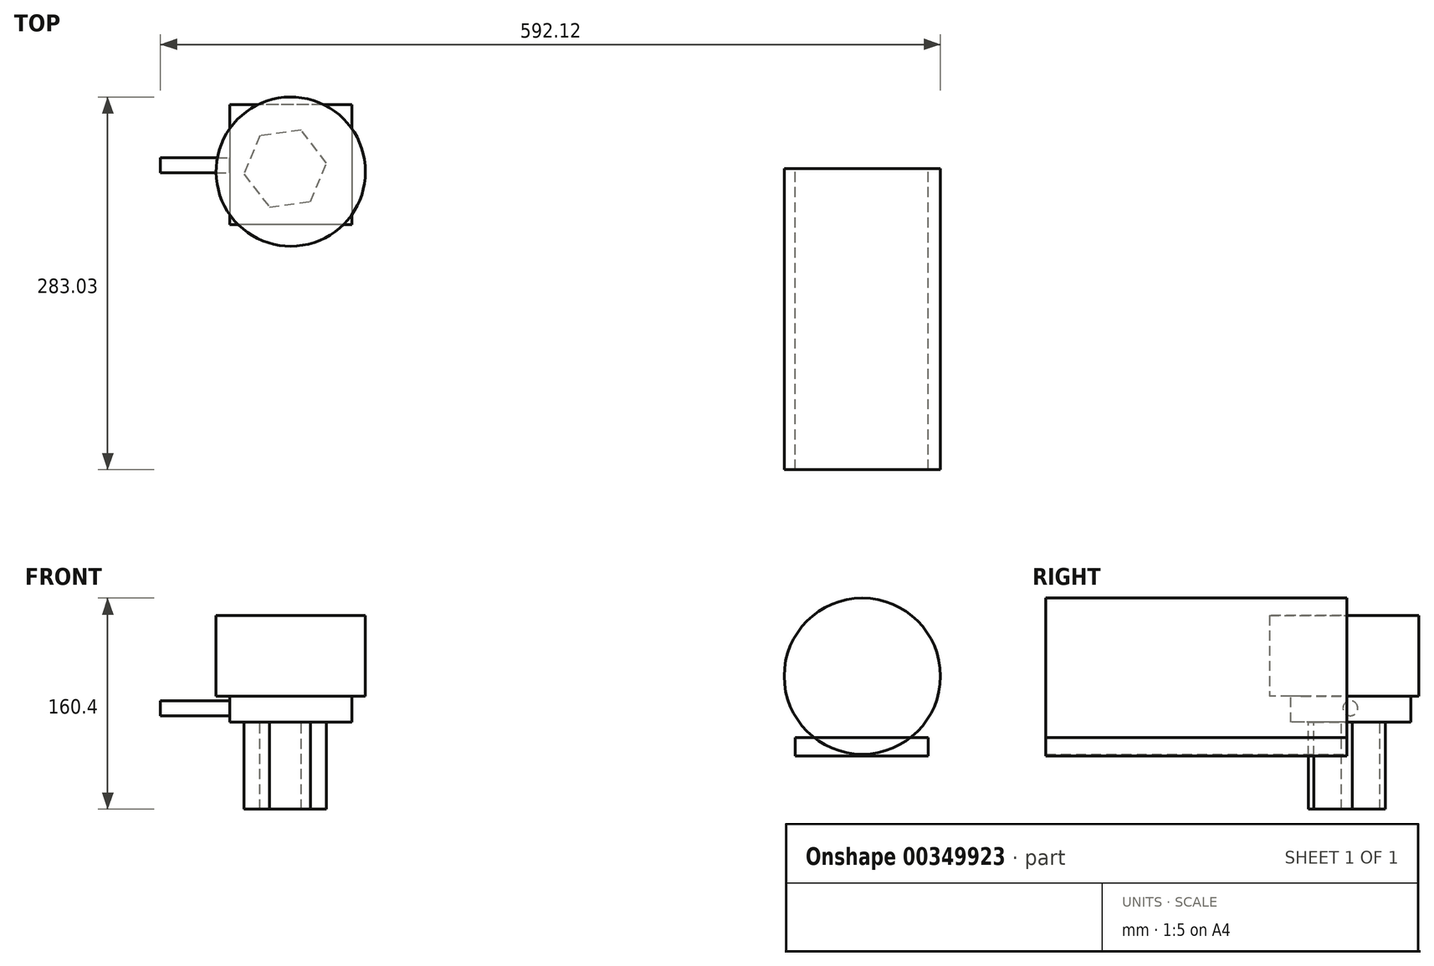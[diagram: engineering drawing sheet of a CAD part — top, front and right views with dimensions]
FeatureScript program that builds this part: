
annotation { "Feature Type Name" : "Feature", "Feature Type Description" : "" }
export const myFeature = defineFeature(function(context is Context, id is Id, definition is map)
    precondition{}
    {
        {
            var Q0;
            Q0=qCreatedBy(makeId("Top.planeOp"),FACE);
            var sketch = newSketch(context, id + "F0", { "sketchPlane" : qUnion([Q0])});
            skCircle(sketch, "E0", {"center": v(0, -2.26) * mm, "radius": 56.68 * mm});
            skSolve(sketch);
        }
        {
            var Q0;
            Q0 = qSketchRegion(id + "F0", true);
            extrude(context, id + "F1", {"entities" : qUnion([Q0]), "depth" : 61.2 * mm, "offsetDistance" : 25.4 * mm});
        }
        {
            var Q0;
            Q0=makeQuery(id+"F1.opExtrude","CAP_FACE",FACE,{"disambiguationData":[OSD([sQuery(id+"F0.wireOp",EDGE,"E0")])],"isStart":true});
            var sketch = newSketch(context, id + "F2", { "sketchPlane" : qUnion([Q0])});
            skLineSegment(sketch, "E1.bottom", {"start": v(46.36, -48.45) * mm, "end": v(-46.36, -48.45) * mm});
            skLineSegment(sketch, "E1.top", {"start": v(46.36, 42.65) * mm, "end": v(-46.36, 42.65) * mm});
            skLineSegment(sketch, "E1.left", {"start": v(46.36, -48.45) * mm, "end": v(46.36, 42.65) * mm});
            skLineSegment(sketch, "E1.right", {"start": v(-46.36, -48.45) * mm, "end": v(-46.36, 42.65) * mm});
            skPoint(sketch, "E1.middle", {"position": v(0, -2.9) * mm});
            skSolve(sketch);
        }
        {
            var Q0;
            Q0 = qSketchRegion(id + "F2", true);
            extrude(context, id + "F3", {"entities" : qUnion([Q0]), "operationType" : NewBodyOperationType.ADD, "depth" : 19.8 * mm, "offsetDistance" : 25.4 * mm});
        }
        {
            var Q0;
            Q0=makeQuery(id+"F3.opExtrude","SWEPT_FACE",FACE,{"disambiguationData":[OSD([sQuery(id+"F2.wireOp",EDGE,"E1.right")])]});
            var sketch = newSketch(context, id + "F4", { "sketchPlane" : qUnion([Q0])});
            skCircle(sketch, "E2", {"center": v(-2.6, -9.2) * mm, "radius": 5.68 * mm});
            skSolve(sketch);
        }
        {
            var Q0;
            Q0 = qSketchRegion(id + "F4", true);
            extrude(context, id + "F5", {"entities" : qUnion([Q0]), "operationType" : NewBodyOperationType.ADD, "depth" : 52.58 * mm, "offsetDistance" : 25.4 * mm});
        }
        {
            var Q0;
            Q0=makeQuery(id+"F3.opExtrude","CAP_FACE",FACE,{"disambiguationData":[OSD([sQuery(id+"F2.wireOp",EDGE,"E1.bottom"),sQuery(id+"F2.wireOp",EDGE,"E1.top"),sQuery(id+"F2.wireOp",EDGE,"E1.left"),sQuery(id+"F2.wireOp",EDGE,"E1.right")])],"isStart":false});
            var sketch = newSketch(context, id + "F6", { "sketchPlane" : qUnion([Q0])});
            skCircle(sketch, "E3.cCircle", {"center": v(-4.2, 0) * mm, "radius": 27.37 * mm, "construction": true});
            skLineSegment(sketch, "E3.0", {"start": v(27.13, -4.2) * mm, "end": v(7.83, -29.23) * mm});
            skLineSegment(sketch, "E3.1", {"start": v(7.83, -29.23) * mm, "end": v(-23.5, -25.02) * mm});
            skLineSegment(sketch, "E3.2", {"start": v(-23.5, -25.02) * mm, "end": v(-35.51, 4.2) * mm});
            skLineSegment(sketch, "E3.3", {"start": v(-35.51, 4.2) * mm, "end": v(-16.21, 29.23) * mm});
            skLineSegment(sketch, "E3.4", {"start": v(-16.21, 29.23) * mm, "end": v(15.11, 25.02) * mm});
            skLineSegment(sketch, "E3.5", {"start": v(15.11, 25.02) * mm, "end": v(27.13, -4.2) * mm});
            skPoint(sketch, "E3.0.midPoint", {"position": v(17.48, -16.72) * mm});
            skSolve(sketch);
        }
        {
            var Q0;
            Q0 = qSketchRegion(id + "F6", true);
            extrude(context, id + "F7", {"entities" : qUnion([Q0]), "operationType" : NewBodyOperationType.ADD, "depth" : 66.04 * mm, "offsetDistance" : 25.4 * mm});
        }
        {
            var Q0;
            Q0=qCreatedBy(makeId("Front.planeOp"),FACE);
            var sketch = newSketch(context, id + "F8", { "sketchPlane" : qUnion([Q0])});
            skCircle(sketch, "E4", {"center": v(258.37, 0) * mm, "radius": 59.3 * mm});
            skLineSegment(sketch, "E5.bottom", {"start": v(382.95, -31.55) * mm, "end": v(484, -31.55) * mm});
            skLineSegment(sketch, "E5.top", {"start": v(382.95, -45.28) * mm, "end": v(484, -45.28) * mm});
            skLineSegment(sketch, "E5.left", {"start": v(382.95, -31.55) * mm, "end": v(382.95, -45.28) * mm});
            skLineSegment(sketch, "E5.right", {"start": v(484, -31.55) * mm, "end": v(484, -45.28) * mm});
            skSolve(sketch);
        }
        {
            var Q0;
            Q0 = qSketchRegion(id + "F8", true);
            extrude(context, id + "F9", {"entities" : qUnion([Q0]), "depth" : 228.6 * mm, "offsetDistance" : 25.4 * mm});
        }
        {
            var Q0;
            Q0=makeQuery(id+"F9.opExtrude","SWEPT_BODY",BODY,{"disambiguationData":[OSD([sQuery(id+"F8.wireOp",EDGE,"E4")])]});
            transform(context, id + "F10", {"entities" : qUnion([Q0]), "transformType" : TransformType.TRANSLATION_3D, "dx" : 175.5 * mm, "dy" : 0 * mm, "dz" : 15.24 * mm, "makeCopy" : false});
        }
    });
